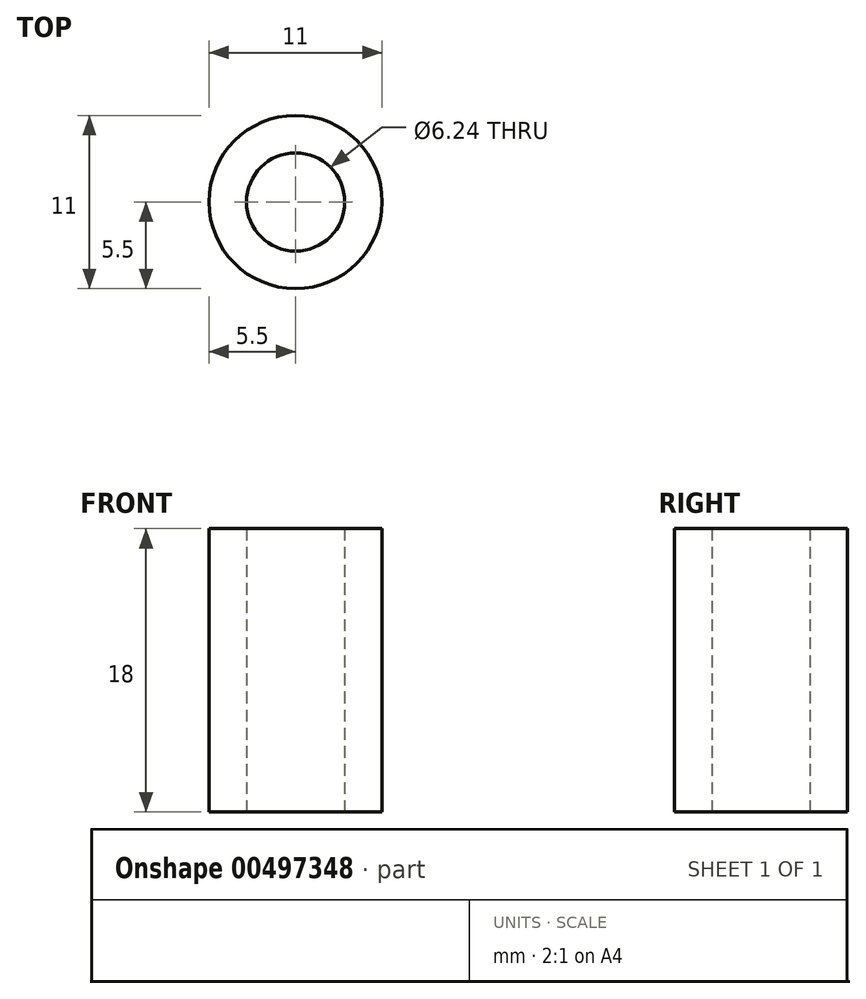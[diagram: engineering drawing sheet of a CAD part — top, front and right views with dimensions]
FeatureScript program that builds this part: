
annotation { "Feature Type Name" : "Feature", "Feature Type Description" : "" }
export const myFeature = defineFeature(function(context is Context, id is Id, definition is map)
    precondition{}
    {
        {
            var Q0;
            Q0=qCreatedBy(makeId("Top.planeOp"), FACE);
            var sketch = newSketch(context, id + "F0", { "sketchPlane" : qUnion([Q0])});
            skCircle(sketch, "E0", {"center": v(0, 0) * mm, "radius": 3.12 * mm});
            skCircle(sketch, "E1", {"center": v(0, 0) * mm, "radius": 5.5 * mm});
            skSolve(sketch);
        }
        {
            var Q0;
            Q0 = qSketchRegion(id + "F0", true);
            extrude(context, id + "F1", {"entities" : qUnion([Q0]), "flatOperationType" : FlatOperationType.REMOVE, "depth" : 18 * mm, "offsetDistance" : 25 * mm, "domain" : OperationDomain.MODEL});
        }
    });
